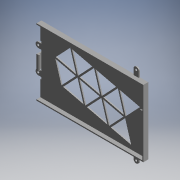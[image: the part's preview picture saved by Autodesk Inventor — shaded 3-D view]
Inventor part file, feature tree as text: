
AUTODESK INVENTOR PART (.ipt)
format: ipt  version: 2019 (Build 230136000, 136)  size: 254,464 bytes
history: native  units: mm (DEFAULTED — no unit token found)
features: extrude x5, sketch x4, projected_geometry x3, chamfer x2
ambient origin geometry x8: Origin, YZ Plane, XZ Plane, XY Plane, X Axis, Y Axis, Z Axis, Center Point
bodies: Solid1 (feature_tree)
feature tree (14):
  sketch  "Sketch1"  dims[d8=3.0mm d9=4.5mm]
  extrude  "Extrusion1"  Depth=4.5mm
  extrude  "Extrusion2"  Depth=1.6mm
  extrude  "Extrusion3"  Depth=7.5mm
  chamfer  "Chamfer1"  Distance=1.6mm
  extrude  "Extrusion4"  Depth=22.5mm
  chamfer  "Chamfer2"  Distance=1.6mm
  extrude  "Extrusion5"  Depth=1.6mm
  sketch  "Sketch2"  dims[d11=1.6mm d14=3.0mm]
  projected_geometry  "Projected Loop1"
  projected_geometry  "Projected Loop2"
  sketch  "Sketch3"  dims[d15=7.5mm d17=7.5mm]
  projected_geometry  "Projected Loop3"
  sketch  "Sketch4"  dims[d19=112.2mm d23=1.6mm d27=22.5mm d28=1.6mm d29=1.6mm d30=149.5mm d31=92.5mm d32=1.6mm d34=140.0mm d36=33.75mm d37=7.5mm d38=1.6mm d39=0.0mm d40=7.0mm d41=0.0mm d42=2.0mm d43=30.0mm d44=3.5mm d45=0.0mm d46=2.0mm d47=2.0mm d48=45.0deg d49=2.2mm d50=2.0mm d51=0.0mm d52=0.75mm d53=2.0mm d54=45.0deg d57=30.0mm d59=35.0mm d60=10.0mm d62=10.0mm d73=5.0mm d76=2.5mm d77=30.0mm d78=30.0mm d80=35.0mm d81=10.0mm d83=10.0mm d85=1.25mm d86=10.0mm d87=0.0mm]
